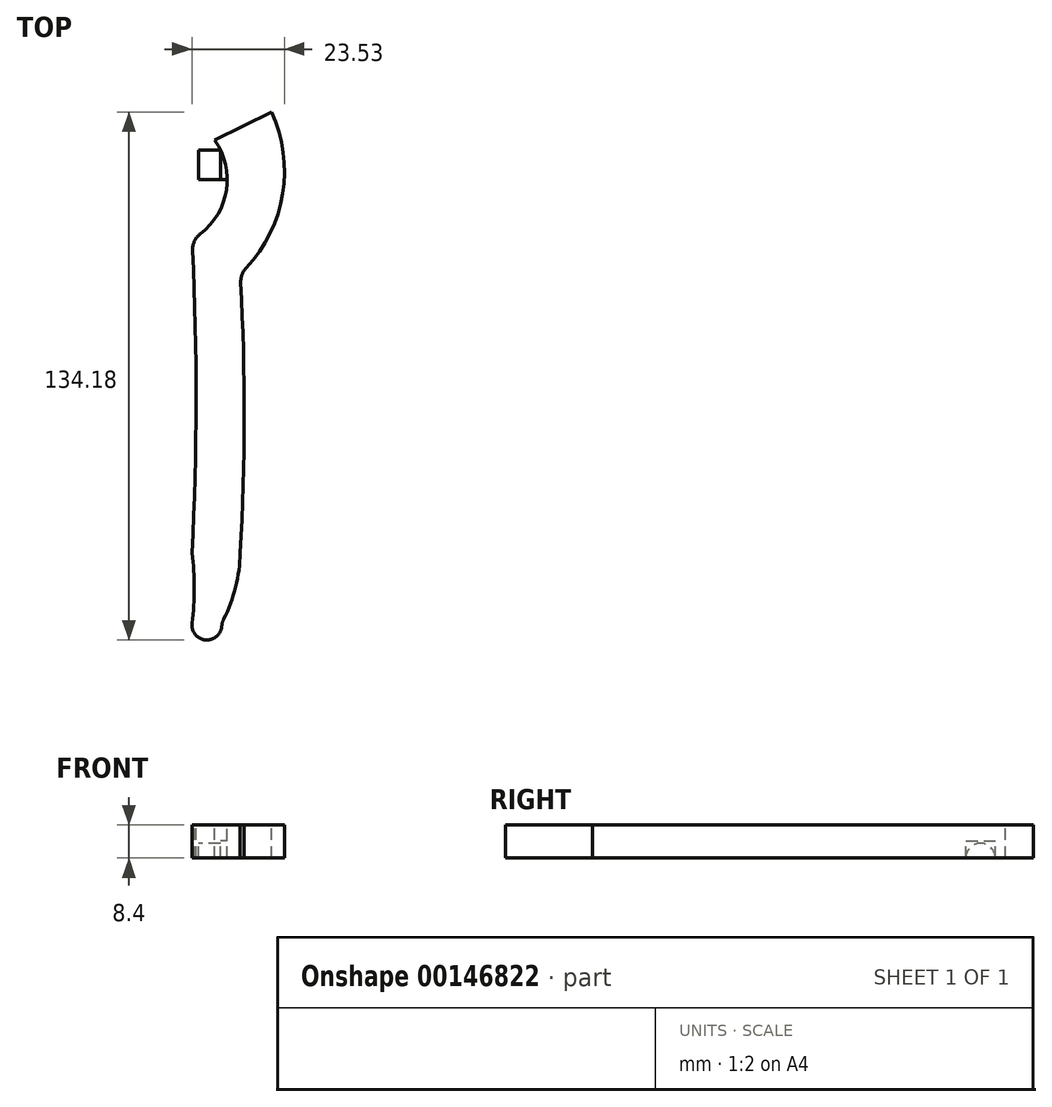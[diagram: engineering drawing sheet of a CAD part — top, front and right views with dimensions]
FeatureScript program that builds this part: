
annotation { "Feature Type Name" : "Feature", "Feature Type Description" : "" }
export const myFeature = defineFeature(function(context is Context, id is Id, definition is map)
    precondition{}
    {
        {
            var Q0;
            Q0=qCreatedBy(makeId("Top.planeOp"),FACE);
            var sketch = newSketch(context, id + "F0", { "sketchPlane" : qUnion([Q0])});
            skArc(sketch, "E0", {"start": v(-18.84, -33.1) * mm, "mid": v(-9.92, -17.2) * mm, "end": v(-18.84, -1.3) * mm});
            skArc(sketch, "E1", {"start": v(-9.22, -40.6) * mm, "mid": v(1.28, -22.3) * mm, "end": v(-0.84, -1.3) * mm});
            skArc(sketch, "E2", {"start": v(-18.84, -111.7) * mm, "mid": v(-17.84, -72.4) * mm, "end": v(-18.84, -33.1) * mm});
            skArc(sketch, "E3", {"start": v(-9.22, -112.4) * mm, "mid": v(-8.2, -76.5) * mm, "end": v(-9.22, -40.6) * mm});
            skArc(sketch, "E4", {"start": v(-18.84, -111.7) * mm, "mid": v(-14.2, -114.48) * mm, "end": v(-9.22, -112.4) * mm});
            skLineSegment(sketch, "E5", {"start": v(-0.84, -1.3) * mm, "end": v(-18.84, -1.3) * mm});
            skArc(sketch, "E6.0", {"start": v(-20.16, -112.1) * mm, "mid": v(-19.14, -72.24) * mm, "end": v(-20.18, -32.37) * mm});
            skLineSegment(sketch, "E6.1", {"start": v(0, 0) * mm, "end": v(-26.43, 0) * mm});
            skArc(sketch, "E6.2", {"start": v(-7.89, -41.14) * mm, "mid": v(2.7, -21.84) * mm, "end": v(0, 0) * mm});
            skArc(sketch, "E6.3", {"start": v(-20.18, -32.37) * mm, "mid": v(-11.53, -13.92) * mm, "end": v(-26.43, 0) * mm});
            skArc(sketch, "E6.4", {"start": v(-7.9, -112.1) * mm, "mid": v(-6.9, -76.62) * mm, "end": v(-7.89, -41.14) * mm});
            skArc(sketch, "E7", {"start": v(-20.16, -129.9) * mm, "mid": v(-19.6, -121) * mm, "end": v(-20.16, -112.1) * mm});
            skArc(sketch, "E8", {"start": v(-12.62, -129.9) * mm, "mid": v(-9.22, -121.28) * mm, "end": v(-7.9, -112.1) * mm});
            skArc(sketch, "E9", {"start": v(-20.16, -129.9) * mm, "mid": v(-16.4, -134.18) * mm, "end": v(-12.62, -129.9) * mm});
            skArc(sketch, "E10", {"start": v(-19.77, -125.92) * mm, "mid": v(-23.95, -127.51) * mm, "end": v(-20.16, -129.9) * mm});
            skCircle(sketch, "E11", {"center": v(-21.46, -127.76) * mm, "radius": 1 * mm});
            skLineSegment(sketch, "E12", {"start": v(-11.22, -17.2) * mm, "end": v(-18.52, -17.2) * mm});
            skLineSegment(sketch, "E13", {"start": v(-18.52, -17.2) * mm, "end": v(-18.52, -9.7) * mm});
            skLineSegment(sketch, "E14", {"start": v(-18.52, -9.7) * mm, "end": v(-12.93, -9.7) * mm});
            skLineSegment(sketch, "E15", {"start": v(0, 0) * mm, "end": v(-14.4, -7.2) * mm});
            skLineSegment(sketch, "E16", {"start": v(30.39, 0) * mm, "end": v(30.39, -148.5) * mm});
            skCircle(sketch, "E17.MirrorC", {"center": v(82.24, -127.76) * mm, "radius": 1 * mm});
            skLineSegment(sketch, "E18.MirrorCS", {"start": v(79.3, -9.7) * mm, "end": v(73.7, -9.7) * mm});
            skLineSegment(sketch, "E19.MirrorCS", {"start": v(72, -17.2) * mm, "end": v(79.3, -17.2) * mm});
            skArc(sketch, "E20.MirrorCS", {"start": v(80.55, -125.92) * mm, "mid": v(84.72, -127.51) * mm, "end": v(80.94, -129.9) * mm});
            skLineSegment(sketch, "E21.MirrorCS", {"start": v(79.3, -17.2) * mm, "end": v(79.3, -9.7) * mm});
            skArc(sketch, "E22.MirrorCS", {"start": v(79.62, -111.7) * mm, "mid": v(74.98, -114.48) * mm, "end": v(70, -112.4) * mm});
            skArc(sketch, "E23.MirrorCS", {"start": v(79.62, -33.1) * mm, "mid": v(70.7, -17.2) * mm, "end": v(79.62, -1.3) * mm});
            skLineSegment(sketch, "E24.MirrorCS", {"start": v(60.78, 0) * mm, "end": v(75.17, -7.2) * mm});
            skArc(sketch, "E25.MirrorCS", {"start": v(73.4, -129.9) * mm, "mid": v(70, -121.28) * mm, "end": v(68.68, -112.1) * mm});
            skArc(sketch, "E26.MirrorCS", {"start": v(80.94, -129.9) * mm, "mid": v(80.37, -121) * mm, "end": v(80.94, -112.1) * mm});
            skArc(sketch, "E27.MirrorCS", {"start": v(68.68, -112.1) * mm, "mid": v(67.69, -76.62) * mm, "end": v(68.66, -41.14) * mm});
            skArc(sketch, "E28.MirrorCS", {"start": v(80.96, -32.37) * mm, "mid": v(72.31, -13.92) * mm, "end": v(87.2, 0) * mm});
            skArc(sketch, "E29.MirrorCS", {"start": v(68.66, -41.14) * mm, "mid": v(58.08, -21.84) * mm, "end": v(60.78, 0) * mm});
            skLineSegment(sketch, "E30.MirrorCS", {"start": v(61.62, -1.3) * mm, "end": v(79.62, -1.3) * mm});
            skLineSegment(sketch, "E31.MirrorCS", {"start": v(60.78, 0) * mm, "end": v(87.2, 0) * mm});
            skArc(sketch, "E32.MirrorCS", {"start": v(80.94, -112.1) * mm, "mid": v(79.92, -72.24) * mm, "end": v(80.96, -32.37) * mm});
            skArc(sketch, "E33.MirrorCS", {"start": v(70, -112.4) * mm, "mid": v(68.99, -76.5) * mm, "end": v(70, -40.6) * mm});
            skArc(sketch, "E34.MirrorCS", {"start": v(79.62, -111.7) * mm, "mid": v(78.62, -72.4) * mm, "end": v(79.62, -33.1) * mm});
            skArc(sketch, "E35.MirrorCS", {"start": v(70, -40.6) * mm, "mid": v(59.5, -22.3) * mm, "end": v(61.62, -1.3) * mm});
            skArc(sketch, "E36.MirrorCS", {"start": v(80.94, -129.9) * mm, "mid": v(77.17, -134.18) * mm, "end": v(73.4, -129.9) * mm});
            skSolve(sketch);
        }
        {
            var Q0;
            {var subQ1=sQuery(id+"F0.wireOp",EDGE,"E1");Q0=makeQuery(id+"F0.imprint","IMPRINT",FACE,{"disambiguationData":[TD([[makeQuery(id+"F0.imprint","IMPRINT",EDGE,{"derivedFrom":subQ1}),1.0]])]});}
            var Q1;
            {var subQ8=sQuery(id+"F0.wireOp",EDGE,"E1");Q1=makeQuery(id+"F0.imprint","IMPRINT",FACE,{"disambiguationData":[TD([[makeQuery(id+"F0.imprint","IMPRINT",EDGE,{"derivedFrom":subQ8}),-1.0]])]});}
            extrude(context, id + "F1", {"entities" : qUnion([Q0, Q1]), "oppositeDirection" : true, "depth" : 8.4 * mm});
        }
        {
            var Q0;
            {var subQ0=sQuery(id+"F0.wireOp",EDGE,"E12");Q0=makeQuery(id+"F0.imprint","IMPRINT",FACE,{"disambiguationData":[TD([[makeQuery(id+"F0.imprint","IMPRINT",EDGE,{"derivedFrom":subQ0}),-1.0]])]});}
            extrude(context, id + "F2", {"entities" : qUnion([Q0]), "operationType" : NewBodyOperationType.ADD, "oppositeDirection" : true, "depth" : 8.4 * mm});
        }
        {
            var Q0;
            {var subQ0=sQuery(id+"F0.wireOp",EDGE,"E12");Q0=makeQuery(id+"F0.imprint","IMPRINT",FACE,{"disambiguationData":[TD([[makeQuery(id+"F0.imprint","IMPRINT",EDGE,{"derivedFrom":subQ0}),-1.0]])]});}
            extrude(context, id + "F3", {"entities" : qUnion([Q0]), "operationType" : NewBodyOperationType.REMOVE, "oppositeDirection" : true, "depth" : 4 * mm});
        }
        {
            var Q0;
            Q0=makeQuery(id+"F2.opExtrude","SWEPT_FACE",FACE,{"disambiguationData":[OSD([sQuery(id+"F0.wireOp",EDGE,"E13")])]});
            var sketch = newSketch(context, id + "F4", { "sketchPlane" : qUnion([Q0])});
            skLineSegment(sketch, "E37.0", {"start": v(17.2, -8.4) * mm, "end": v(9.7, -8.4) * mm});
            skLineSegment(sketch, "E37.1", {"start": v(17.2, -8.4) * mm, "end": v(17.2, -4) * mm});
            skLineSegment(sketch, "E37.2", {"start": v(17.2, -4) * mm, "end": v(9.7, -4) * mm});
            skLineSegment(sketch, "E37.3", {"start": v(9.7, -8.4) * mm, "end": v(9.7, -4) * mm});
            skArc(sketch, "E38", {"start": v(17.2, -8.4) * mm, "mid": v(13.45, -4.65) * mm, "end": v(9.7, -8.4) * mm});
            skSolve(sketch);
        }
        {
            var Q0;
            Q0=makeQuery(id+"F4.imprint","IMPRINT",FACE,{"disambiguationData":[TD([[makeQuery(id+"F4.imprint","IMPRINT",EDGE,{"derivedFrom":sQuery(id+"F4.wireOp",EDGE,"E37.1")}),1.0]])]});
            extrude(context, id + "F5", {"entities" : qUnion([Q0]), "operationType" : NewBodyOperationType.REMOVE, "oppositeDirection" : true, "depth" : 5.6 * mm});
        }
        {
            var Q0;
            Q0=makeQuery(id+"F1.opExtrude","SWEPT_EDGE",EDGE,{"disambiguationData":[OSD([sQuery(id+"F0.wireOp",EDGE,"E6.2"),sQuery(id+"F0.wireOp",EDGE,"E6.4")])]});
            var Q1;
            Q1=makeQuery(id+"F1.opExtrude","SWEPT_EDGE",EDGE,{"disambiguationData":[OSD([sQuery(id+"F0.wireOp",EDGE,"E6.0"),sQuery(id+"F0.wireOp",EDGE,"E6.3")])]});
            var Q2;
            Q2=makeQuery(id+"F1.opExtrude","SWEPT_EDGE",EDGE,{"disambiguationData":[OSD([sQuery(id+"F0.wireOp",EDGE,"E8"),sQuery(id+"F0.wireOp",EDGE,"E9")])]});
            fillet(context, id + "F6", {"entities" : qUnion([Q0, Q1, Q2]), "radius" : 5 * mm, "tangentPropagation" : true, "allowEdgeOverflow" : false});
        }
    });
